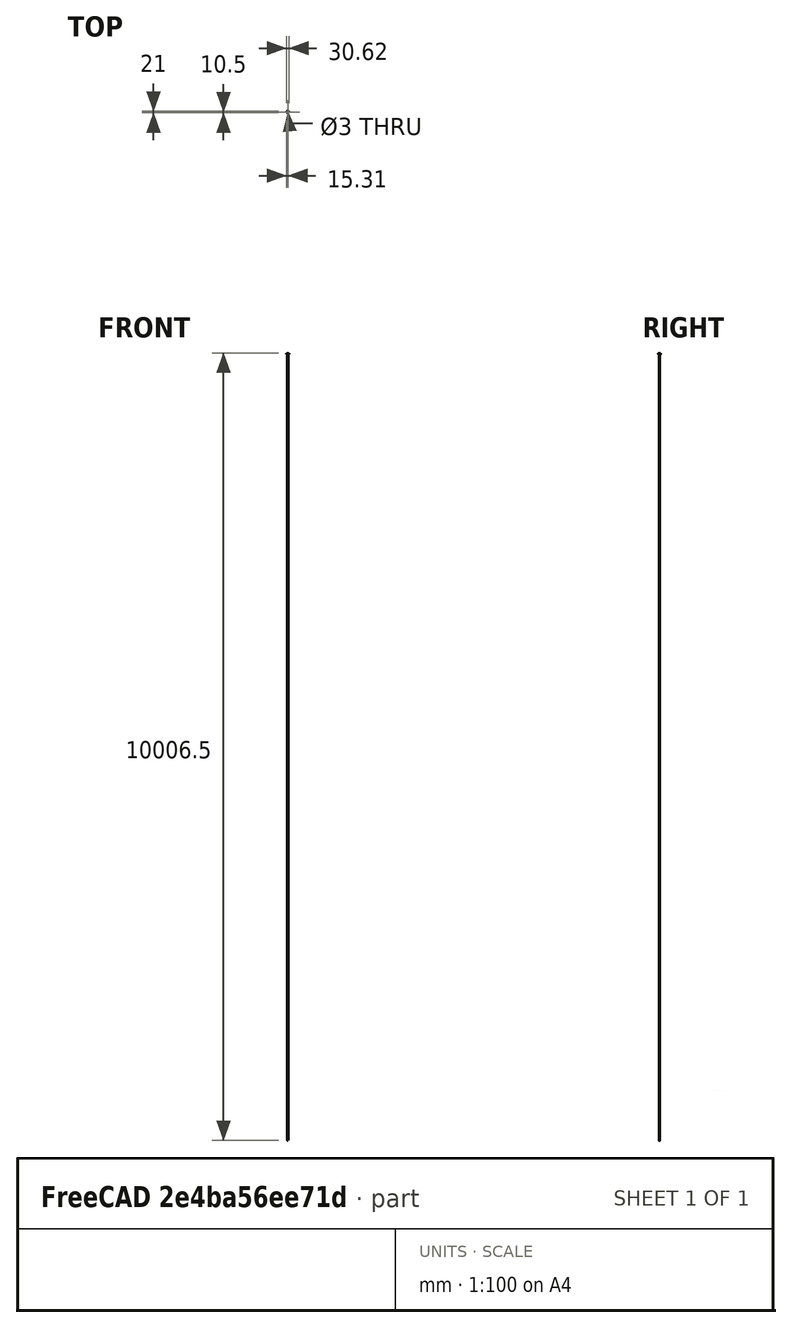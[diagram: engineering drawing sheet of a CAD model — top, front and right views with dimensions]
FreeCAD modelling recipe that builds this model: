
FCSTD DOCUMENT  (FreeCAD 0.16R)
Label: KetchupA118
License: All rights reserved
LicenseURL: http://en.wikipedia.org/wiki/All_rights_reserved
objects: Sketcher::SketchObject×5, PartDesign::Pocket×3, Part::Cut×2, PartDesign::Fillet×2, PartDesign::Pad×1, PartDesign::Revolution×1, Part::Sphere×1, Part::Box×1, Mesh::Feature×1
note: 21 computed .brp shape members not serialized (recipe doc carries the construction recipe); baked Part::Feature solids carry a one-line shape summary decoded from their .brp

FEATURE [Sketcher::SketchObject] Sketch
  sketch-geometry (4):
    g0: LineSegment StartX=-3.625 StartY=3.625 StartZ=0 EndX=3.625 EndY=3.625 EndZ=0
    g1: LineSegment StartX=3.625 StartY=3.625 StartZ=0 EndX=3.625 EndY=-3.625 EndZ=0
    g2: LineSegment StartX=3.625 StartY=-3.625 StartZ=0 EndX=-3.625 EndY=-3.625 EndZ=0
    g3: LineSegment StartX=-3.625 StartY=-3.625 StartZ=0 EndX=-3.625 EndY=3.625 EndZ=0
  constraints (11):
    c: Coincident(g0,g1)
    c: Coincident(g1,g2)
    c: Coincident(g2,g3)
    c: Coincident(g3,g0)
    c: Horizontal(g0)
    c: Horizontal(g2)
    c: Vertical(g1)
    c: Vertical(g3)
    c: Symmetric(g1,g0,g-1)
    c: Equal(g1,g0)
    c: Distance(g1) = 7.25
FEATURE [PartDesign::Pad] Pad
  Length = 16
  Length2 = 100
  Sketch = -> Sketch
  Type = 0
FEATURE [Sketcher::SketchObject] Sketch003
  Placement = pos=(0,0,16) rot=(0,0,1;0rad)
  Support = -> Pad [Face6]
  sketch-geometry (2):
    g0: ArcOfCircle CenterX=0 CenterY=0 CenterZ=0 NormalX=0 NormalY=0 NormalZ=1 Radius=10.5 StartAngle=0 EndAngle=3.14159
    g1: LineSegment StartX=-10.5 StartY=0 StartZ=0 EndX=10.5 EndY=0 EndZ=0
  constraints (6):
    c: Coincident(g0,g-1)
    c: PointOnObject(g0,g-1)
    c: PointOnObject(g0,g-1)
    c: Radius(g0) = 10.5
    c: Coincident(g1,g0)
    c: Coincident(g1,g0)
FEATURE [PartDesign::Revolution] Revolution
  Angle = 360
  Axis = (1,0,0)
  Base = (0,0,16)
  ReferenceAxis = -> Sketch003 [H_Axis]
  Reversed = true
  Sketch = -> Sketch003
FEATURE [Part::Sphere] Sphere
  Angle1 = -90
  Angle2 = 90
  Angle3 = 360
  Placement = pos=(0,0,18) rot=(0,0,1;0rad)
  Radius = 8.5
FEATURE [Part::Cut] Cut
  Base = -> Revolution
  Tool = -> Sphere
FEATURE [Part::Box] Box  label="Cube"
  Height = 30
  Length = 30
  Placement = pos=(-15,-15,20) rot=(0,0,1;0rad)
  Width = 30
FEATURE [Part::Cut] Cut001
  Base = -> Cut
  Tool = -> Box
FEATURE [Sketcher::SketchObject] Sketch006
  Placement = pos=(0,0,20) rot=(0,0,1;0rad)
  Support = -> Cut001 [Face7]
  sketch-geometry (1):
    g0: Circle CenterX=0 CenterY=0 CenterZ=0 NormalX=0 NormalY=0 NormalZ=1 Radius=1.5
  constraints (2):
    c: Radius(g0) = 1.5
    c: Coincident(g0,g-1)
FEATURE [PartDesign::Pocket] Pocket
  Length = 5
  Sketch = -> Sketch006
  Type = 1
FEATURE [Sketcher::SketchObject] Sketch005
  Placement = pos=(0,0,20) rot=(0,0,1;0rad)
  Support = -> Pocket [Face9]
  sketch-geometry (4):
    g0: LineSegment StartX=-15.3059 StartY=0.75 StartZ=0 EndX=15.3059 EndY=0.75 EndZ=0
    g1: LineSegment StartX=15.3059 StartY=0.75 StartZ=0 EndX=15.3059 EndY=-0.75 EndZ=0
    g2: LineSegment StartX=15.3059 StartY=-0.75 StartZ=0 EndX=-15.3059 EndY=-0.75 EndZ=0
    g3: LineSegment StartX=-15.3059 StartY=-0.75 StartZ=0 EndX=-15.3059 EndY=0.75 EndZ=0
  constraints (10):
    c: Coincident(g0,g1)
    c: Coincident(g1,g2)
    c: Coincident(g2,g3)
    c: Coincident(g3,g0)
    c: Horizontal(g0)
    c: Horizontal(g2)
    c: Vertical(g1)
    c: Vertical(g3)
    c: Symmetric(g1,g0,g-1)
    c: Distance(g1) = 1.5
FEATURE [PartDesign::Pocket] Pocket001
  Length = 7
  Sketch = -> Sketch005
  Type = 0
FEATURE [Sketcher::SketchObject] Sketch004
  Placement = pos=(0,0,20) rot=(0,0,1;0rad)
  Support = -> Pocket001 [Face17]
  sketch-geometry (4):
    g0: LineSegment StartX=-0.75 StartY=13.7981 StartZ=0 EndX=0.75 EndY=13.7981 EndZ=0
    g1: LineSegment StartX=0.75 StartY=13.7981 StartZ=0 EndX=0.75 EndY=-13.7981 EndZ=0
    g2: LineSegment StartX=0.75 StartY=-13.7981 StartZ=0 EndX=-0.75 EndY=-13.7981 EndZ=0
    g3: LineSegment StartX=-0.75 StartY=-13.7981 StartZ=0 EndX=-0.75 EndY=13.7981 EndZ=0
  constraints (11):
    c: Coincident(g0,g1)
    c: Coincident(g1,g2)
    c: Coincident(g2,g3)
    c: Coincident(g3,g0)
    c: Horizontal(g0)
    c: Horizontal(g2)
    c: Vertical(g1)
    c: Vertical(g3)
    c: Symmetric(g1,g2,g-2)
    c: Distance(g0) = 1.5
    c: Symmetric(g1,g0,g-1)
FEATURE [PartDesign::Pocket] Pocket002
  Length = 7
  Sketch = -> Sketch004
  Type = 0
FEATURE [PartDesign::Fillet] Fillet
  Base = -> Pocket002 [Edge39,Edge35,Edge47,Edge43,Edge71,Edge19,Edge23,Edge64,Edge67,Edge68,Edge53,Edge60,Edge51,Edge57,Edge61,Edge56]
  Radius = 0.29
FEATURE [PartDesign::Fillet] Fillet001
  Base = -> Fillet [Edge28,Edge26,Edge25,Edge27]
  Radius = 5
FEATURE [Mesh::Feature] Mesh  label="Fillet001 (Meshed)"
